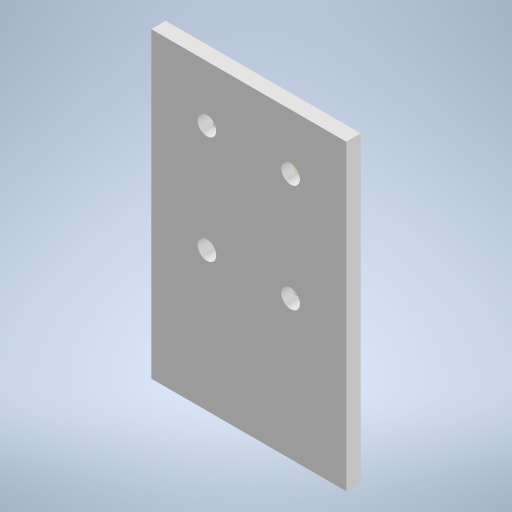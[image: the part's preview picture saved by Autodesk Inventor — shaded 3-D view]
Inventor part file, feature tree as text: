
AUTODESK INVENTOR PART (.ipt)
format: ipt  version: 2023.2 (Build 272271030, 271C)  size: 465,920 bytes
history: native  units: in
note: dims shown in document units (in); Inventor stores cm internally (conversion verified against a paired STEP export)
features: sketch x4, extrude x3, other x3, plane x1, emboss x1, reference x1
ambient origin geometry x8: Origin, YZ Plane, XZ Plane, XY Plane, X Axis, Y Axis, Z Axis, Center Point
bodies: Solid1 (feature_tree)
feature tree (13):
  plane  "Work Plane1"
  extrude  "Extrusion1"  Depth=0.0039in
  extrude  "Extrusion2"  Depth=0.0039in
  extrude  "Extrusion3"  Depth=2.5in
  emboss  "Emboss1"
  sketch  "Sketch1"  dims[d0=0.0039in d1=0.0039in]
  reference  "Reference1"
  sketch  "Sketch2"  dims[d2=0.0039in d3=0.0039in]
  sketch  "Sketch3"  dims[d4=0.0039in d5=2.5in]
  sketch  "Sketch4"  dims[d6=1.0in d7=1.0in d8=1.0in d9=0.063in d10=0.0in d11=0.1969in d12=0.0in d13=0.0in d14=0.0in d15=0.0079in d16=0.0in]
  other  "<userpath>\Dropbox\elec\Mechanical\NanoBoxArray\_Tooling_PCBPaste.iam"
  other  "_Tooling_PCBPaste.iam"
  other  "nanobox_v31_upgrade_BOARD:1"
